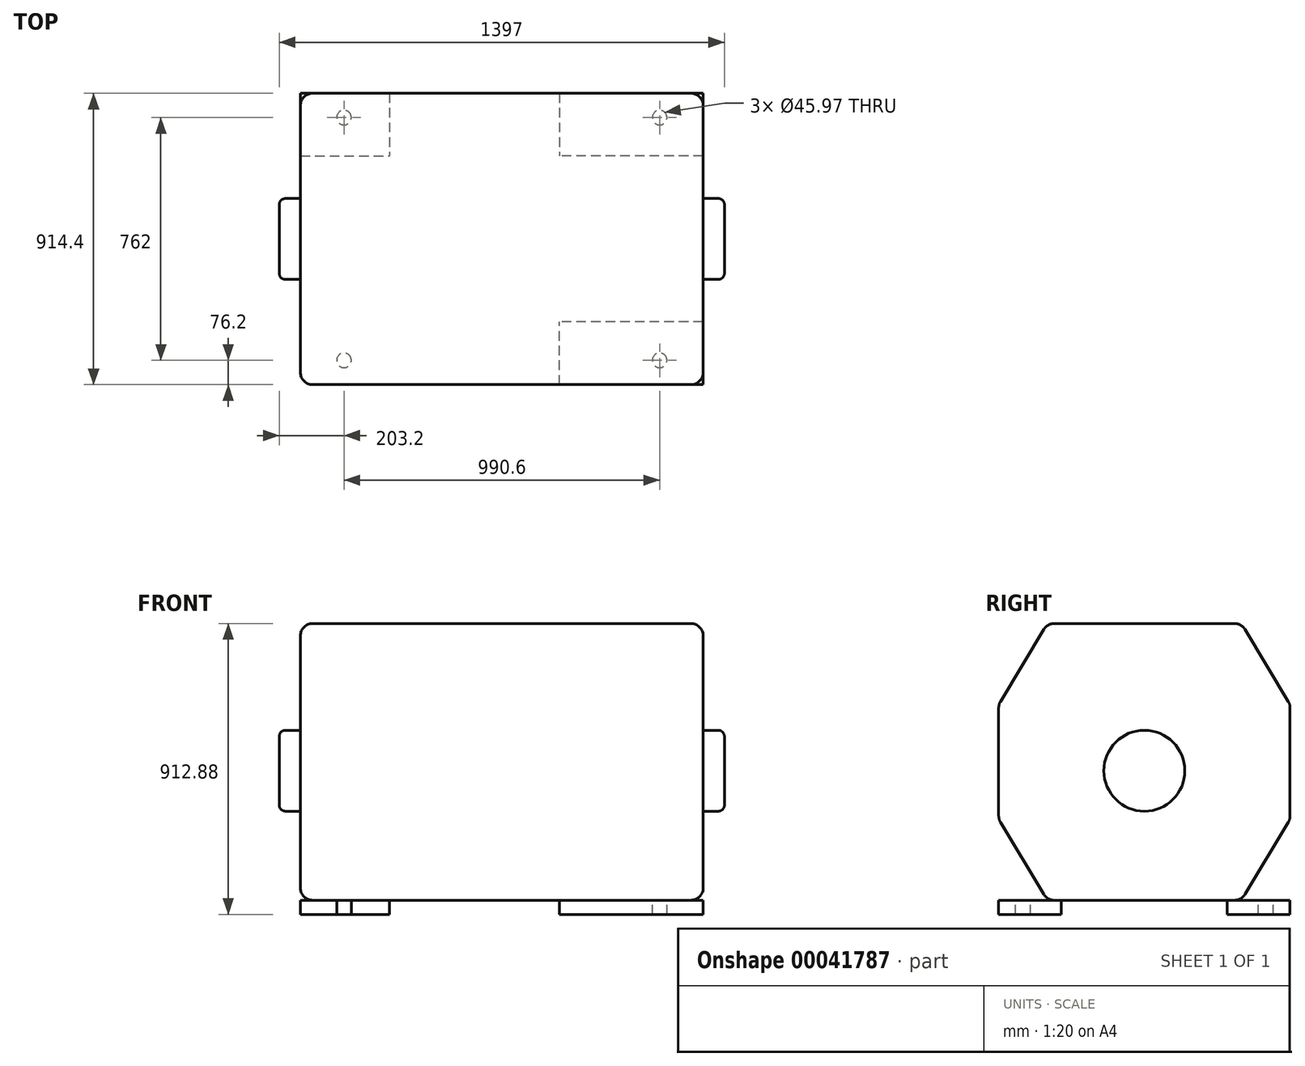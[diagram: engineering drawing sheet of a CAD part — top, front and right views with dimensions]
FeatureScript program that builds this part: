
annotation { "Feature Type Name" : "Feature", "Feature Type Description" : "" }
export const myFeature = defineFeature(function(context is Context, id is Id, definition is map)
    precondition{}
    {
        {
            var Q0;
            Q0=qCreatedBy(makeId("Top.planeOp"),FACE);
            var sketch = newSketch(context, id + "F0", { "sketchPlane" : qUnion([Q0])});
            skLineSegment(sketch, "E0.rect.bottom", {"start": v(-631.83, 457.2) * mm, "end": v(631.83, 457.2) * mm, "construction": true});
            skLineSegment(sketch, "E0.rect.top", {"start": v(-631.83, -457.2) * mm, "end": v(631.83, -457.2) * mm, "construction": true});
            skLineSegment(sketch, "E0.rect.left", {"start": v(-631.82, 457.2) * mm, "end": v(-631.83, -457.2) * mm, "construction": true});
            skLineSegment(sketch, "E0.rect.right", {"start": v(631.83, 457.2) * mm, "end": v(631.83, -457.2) * mm, "construction": true});
            skPoint(sketch, "E0.rect.middle", {"position": v(0, 0) * mm});
            skLineSegment(sketch, "E1.bottom", {"start": v(-631.83, 457.2) * mm, "end": v(-352.43, 457.2) * mm});
            skLineSegment(sketch, "E1.top", {"start": v(-631.83, 260.35) * mm, "end": v(-352.43, 260.35) * mm});
            skLineSegment(sketch, "E1.left", {"start": v(-631.83, 457.2) * mm, "end": v(-631.83, 260.35) * mm});
            skLineSegment(sketch, "E1.right", {"start": v(-352.43, 457.2) * mm, "end": v(-352.43, 260.35) * mm});
            skLineSegment(sketch, "E2.bottom", {"start": v(631.83, 457.2) * mm, "end": v(180.98, 457.2) * mm});
            skLineSegment(sketch, "E2.top", {"start": v(631.83, 260.35) * mm, "end": v(180.98, 260.35) * mm});
            skLineSegment(sketch, "E2.left", {"start": v(631.83, 457.2) * mm, "end": v(631.83, 260.35) * mm});
            skLineSegment(sketch, "E2.right", {"start": v(180.98, 457.2) * mm, "end": v(180.98, 260.35) * mm});
            skLineSegment(sketch, "E3", {"start": v(0, 476.86) * mm, "end": v(0, -472.8) * mm, "construction": true});
            skLineSegment(sketch, "E4", {"start": v(-689.14, 0) * mm, "end": v(696.03, 0) * mm, "construction": true});
            skPoint(sketch, "E4.endSnap0", {"position": v(631.83, 0) * mm});
            skLineSegment(sketch, "E5.0", {"start": v(-495.3, 476.86) * mm, "end": v(-495.3, -472.8) * mm, "construction": true});
            skLineSegment(sketch, "E6.0", {"start": v(-689.14, 381) * mm, "end": v(696.03, 381) * mm, "construction": true});
            skCircle(sketch, "E7", {"center": v(-495.3, 381) * mm, "radius": 22.99 * mm});
            skCircle(sketch, "E8.MirrorC", {"center": v(495.3, 381) * mm, "radius": 22.99 * mm});
            skCircle(sketch, "E9.MirrorC", {"center": v(-495.3, -381) * mm, "radius": 22.99 * mm});
            skLineSegment(sketch, "E10.MirrorCS", {"start": v(-631.83, -457.2) * mm, "end": v(-631.83, -260.35) * mm});
            skLineSegment(sketch, "E11.MirrorCS", {"start": v(-631.83, -260.35) * mm, "end": v(-352.43, -260.35) * mm});
            skLineSegment(sketch, "E12.MirrorCS", {"start": v(-352.43, -457.2) * mm, "end": v(-352.43, -260.35) * mm});
            skLineSegment(sketch, "E13.MirrorCS", {"start": v(-631.83, -457.2) * mm, "end": v(-352.43, -457.2) * mm});
            skLineSegment(sketch, "E14.MirrorCS", {"start": v(631.83, -457.2) * mm, "end": v(180.98, -457.2) * mm});
            skLineSegment(sketch, "E15.MirrorCS", {"start": v(631.83, -260.35) * mm, "end": v(180.98, -260.35) * mm});
            skLineSegment(sketch, "E16.MirrorCS", {"start": v(180.98, -457.2) * mm, "end": v(180.98, -260.35) * mm});
            skLineSegment(sketch, "E17.MirrorCS", {"start": v(631.83, -457.2) * mm, "end": v(631.83, -260.35) * mm});
            skLineSegment(sketch, "E18.MirrorCS", {"start": v(-631.83, -457.2) * mm, "end": v(631.83, -457.2) * mm});
            skLineSegment(sketch, "E19.MirrorCS", {"start": v(-689.14, -381) * mm, "end": v(696.03, -381) * mm, "construction": true});
            skCircle(sketch, "E20.MirrorC", {"center": v(495.3, -381) * mm, "radius": 22.99 * mm});
            skSolve(sketch);
        }
        {
            var Q0;
            Q0=makeQuery(id+"F0.imprint","IMPRINT",FACE,{"disambiguationData":[TD([[makeQuery(id+"F0.imprint","IMPRINT",EDGE,{"derivedFrom":sQuery(id+"F0.wireOp",EDGE,"E1.bottom")}),-1.0]])]});
            var Q1;
            Q1=makeQuery(id+"F0.imprint","IMPRINT",FACE,{"disambiguationData":[TD([[makeQuery(id+"F0.imprint","IMPRINT",EDGE,{"derivedFrom":sQuery(id+"F0.wireOp",EDGE,"E2.bottom")}),1.0]])]});
            var Q2;
            Q2=makeQuery(id+"F0.imprint","IMPRINT",FACE,{"disambiguationData":[TD([[makeQuery(id+"F0.imprint","IMPRINT",EDGE,{"derivedFrom":sQuery(id+"F0.wireOp",EDGE,"E15.MirrorCS")}),1.0]])]});
            var Q3;
            Q3=makeQuery(id+"F0.imprint","IMPRINT",FACE,{"disambiguationData":[TD([[makeQuery(id+"F0.imprint","IMPRINT",EDGE,{"derivedFrom":sQuery(id+"F0.wireOp",EDGE,"E9.MirrorC")}),1.0]])]});
            extrude(context, id + "F1", {"entities" : qUnion([Q0, Q1, Q2, Q3]), "oppositeDirection" : true, "depth" : 44.45 * mm});
        }
        {
            var Q0;
            Q0=qCreatedBy(makeId("Top.planeOp"),FACE);
            var sketch = newSketch(context, id + "F2", { "sketchPlane" : qUnion([Q0])});
            skLineSegment(sketch, "E21.0", {"start": v(-631.83, 457.2) * mm, "end": v(-352.43, 457.2) * mm, "construction": true});
            skLineSegment(sketch, "E22.0", {"start": v(180.98, -457.2) * mm, "end": v(631.83, -457.2) * mm, "construction": true});
            skLineSegment(sketch, "E23.bottom", {"start": v(-631.83, 457.2) * mm, "end": v(631.83, 457.2) * mm});
            skLineSegment(sketch, "E23.top", {"start": v(-631.83, -457.2) * mm, "end": v(631.83, -457.2) * mm});
            skLineSegment(sketch, "E23.left", {"start": v(-631.83, 457.2) * mm, "end": v(-631.83, -457.2) * mm});
            skLineSegment(sketch, "E23.right", {"start": v(631.83, 457.2) * mm, "end": v(631.83, -457.2) * mm});
            skSolve(sketch);
        }
        {
            var Q0;
            Q0=makeQuery(id+"F2.imprint","IMPRINT",FACE,{"disambiguationData":[TD([[makeQuery(id+"F2.imprint","IMPRINT",EDGE,{"derivedFrom":sQuery(id+"F2.wireOp",EDGE,"E23.bottom")}),-1.0]])]});
            extrude(context, id + "F3", {"entities" : qUnion([Q0]), "depth" : 868.43 * mm});
        }
        {
            var Q0;
            Q0=makeQuery(id+"F3.opExtrude","CAP_EDGE",EDGE,{"disambiguationData":[OSD([sQuery(id+"F2.wireOp",EDGE,"E23.top")])],"isStart":false});
            var Q1;
            Q1=makeQuery(id+"F3.opExtrude","CAP_EDGE",EDGE,{"disambiguationData":[OSD([sQuery(id+"F2.wireOp",EDGE,"E23.top")])],"isStart":true});
            var Q2;
            Q2=makeQuery(id+"F3.opExtrude","CAP_EDGE",EDGE,{"disambiguationData":[OSD([sQuery(id+"F2.wireOp",EDGE,"E23.bottom")])],"isStart":false});
            var Q3;
            Q3=makeQuery(id+"F3.opExtrude","CAP_EDGE",EDGE,{"disambiguationData":[OSD([sQuery(id+"F2.wireOp",EDGE,"E23.bottom")])],"isStart":true});
            chamfer(context, id + "F4", {"entities" : qUnion([Q0, Q1, Q2, Q3]), "chamferType" : ChamferType.TWO_OFFSETS, "width1" : 152.4 * mm, "oppositeDirection" : false, "width2" : 254 * mm, "tangentPropagation" : true});
        }
        {
            var Q0;
            Q0=makeQuery(id+"F3.opExtrude","SWEPT_FACE",FACE,{"disambiguationData":[OSD([sQuery(id+"F2.wireOp",EDGE,"E23.left")])]});
            var Q1;
            Q1=makeQuery(id+"F3.opExtrude","SWEPT_FACE",FACE,{"disambiguationData":[OSD([sQuery(id+"F2.wireOp",EDGE,"E23.right")])]});
            var Q2;
            {var subQ0=sQuery(id+"F2.wireOp",EDGE,"E23.bottom");Q2=makeQuery(id+"F4.opChamfer","BLEND_EDGE",EDGE,{"blendedFrom":[makeQuery(id+"F3.opExtrude","CAP_EDGE",EDGE,{"disambiguationData":[OSD([subQ0])],"isStart":true}),makeQuery(id+"F3.opExtrude","CAP_FACE",FACE,{"disambiguationData":[OSD([subQ0,sQuery(id+"F2.wireOp",EDGE,"E23.top"),sQuery(id+"F2.wireOp",EDGE,"E23.left"),sQuery(id+"F2.wireOp",EDGE,"E23.right")])],"isStart":true})],"blendedInto":[makeQuery(id+"F3.opExtrude","CAP_FACE",FACE,{"disambiguationData":[OSD([subQ0,sQuery(id+"F2.wireOp",EDGE,"E23.top"),sQuery(id+"F2.wireOp",EDGE,"E23.left"),sQuery(id+"F2.wireOp",EDGE,"E23.right")])],"isStart":true})]});}
            var Q3;
            {var subQ0=sQuery(id+"F2.wireOp",EDGE,"E23.bottom");Q3=makeQuery(id+"F4.opChamfer","BLEND_EDGE",EDGE,{"blendedFrom":[makeQuery(id+"F3.opExtrude","CAP_EDGE",EDGE,{"disambiguationData":[OSD([subQ0])],"isStart":true}),makeQuery(id+"F3.opExtrude","SWEPT_FACE",FACE,{"disambiguationData":[OSD([subQ0])]})],"blendedInto":[makeQuery(id+"F3.opExtrude","SWEPT_FACE",FACE,{"disambiguationData":[OSD([subQ0])]})]});}
            var Q4;
            Q4=makeQuery(id+"F3.opExtrude","SWEPT_FACE",FACE,{"disambiguationData":[OSD([sQuery(id+"F2.wireOp",EDGE,"E23.bottom")])]});
            var Q5;
            {var subQ0=sQuery(id+"F2.wireOp",EDGE,"E23.bottom");Q5=makeQuery(id+"F4.opChamfer","BLEND_FACE",FACE,{"disambiguationData":[OSD([subQ0]),TDD([makeQuery(id+"F3.opExtrude","CAP_EDGE",EDGE,{"disambiguationData":[OSD([subQ0])],"isStart":false})])]});}
            var Q6;
            Q6=makeQuery(id+"F3.opExtrude","CAP_FACE",FACE,{"disambiguationData":[OSD([sQuery(id+"F2.wireOp",EDGE,"E23.bottom"),sQuery(id+"F2.wireOp",EDGE,"E23.top"),sQuery(id+"F2.wireOp",EDGE,"E23.left"),sQuery(id+"F2.wireOp",EDGE,"E23.right")])],"isStart":false});
            var Q7;
            {var subQ0=sQuery(id+"F2.wireOp",EDGE,"E23.top");Q7=makeQuery(id+"F4.opChamfer","BLEND_FACE",FACE,{"disambiguationData":[OSD([subQ0]),TDD([makeQuery(id+"F3.opExtrude","CAP_EDGE",EDGE,{"disambiguationData":[OSD([subQ0])],"isStart":false})])]});}
            var Q8;
            Q8=makeQuery(id+"F3.opExtrude","SWEPT_FACE",FACE,{"disambiguationData":[OSD([sQuery(id+"F2.wireOp",EDGE,"E23.top")])]});
            var Q9;
            {var subQ0=sQuery(id+"F2.wireOp",EDGE,"E23.top");Q9=makeQuery(id+"F4.opChamfer","BLEND_FACE",FACE,{"disambiguationData":[OSD([subQ0]),TDD([makeQuery(id+"F3.opExtrude","CAP_EDGE",EDGE,{"disambiguationData":[OSD([subQ0])],"isStart":true})])]});}
            fillet(context, id + "F5", {"entities" : qUnion([Q0, Q1, Q2, Q3, Q4, Q5, Q6, Q7, Q8, Q9]), "radius" : 38.1 * mm, "tangentPropagation" : true, "allowEdgeOverflow" : false});
        }
        {
            var Q0;
            Q0=makeQuery(id+"F3.opExtrude","SWEPT_FACE",FACE,{"disambiguationData":[OSD([sQuery(id+"F2.wireOp",EDGE,"E23.right")])]});
            var sketch = newSketch(context, id + "F6", { "sketchPlane" : qUnion([Q0])});
            skLineSegment(sketch, "E24.0", {"start": v(-457.2, -44.45) * mm, "end": v(-260.35, -44.45) * mm, "construction": true});
            skLineSegment(sketch, "E25", {"start": v(0, 0) * mm, "end": v(0, 978.78) * mm, "construction": true});
            skLineSegment(sketch, "E26.0", {"start": v(-457.2, 406.4) * mm, "end": v(0, 406.4) * mm, "construction": true});
            skCircle(sketch, "E27", {"center": v(0, 406.4) * mm, "radius": 127 * mm});
            skSolve(sketch);
        }
        {
            var Q0;
            Q0=qSketchRegion(id+"F6",true);
            extrude(context, id + "F7", {"entities" : qUnion([Q0]), "depth" : 66.67 * mm});
        }
        {
            var Q0;
            Q0=makeQuery(id+"F7.opExtrude","SWEPT_BODY",BODY,{"disambiguationData":[OSD([sQuery(id+"F6.wireOp",EDGE,"E27")])]});
            var Q1;
            Q1=qCreatedBy(makeId("Right.planeOp"),FACE);
            mirror(context, id + "F8", {"operationType" : NewBodyOperationType.ADD, "entities" : qUnion([Q0]), "mirrorPlane" : qUnion([Q1])});
        }
        {
            var Q0;
            Q0=makeQuery(id+"F7.opExtrude","CAP_EDGE",EDGE,{"disambiguationData":[OSD([sQuery(id+"F6.wireOp",EDGE,"E27")])],"isStart":true});
            var Q1;
            Q1=makeQuery(id+"F7.opExtrude","CAP_EDGE",EDGE,{"disambiguationData":[OSD([sQuery(id+"F6.wireOp",EDGE,"E27")])],"isStart":false});
            var Q2;
            Q2=makeQuery(id+"F8.opPattern","COPY",EDGE,{"derivedFrom":makeQuery(id+"F7.opExtrude","CAP_EDGE",EDGE,{"disambiguationData":[OSD([sQuery(id+"F6.wireOp",EDGE,"E27")])],"isStart":false}),"instanceName":"1"});
            var Q3;
            Q3=makeQuery(id+"F8.opPattern","COPY",EDGE,{"derivedFrom":makeQuery(id+"F7.opExtrude","CAP_EDGE",EDGE,{"disambiguationData":[OSD([sQuery(id+"F6.wireOp",EDGE,"E27")])],"isStart":true}),"instanceName":"1"});
            fillet(context, id + "F9", {"entities" : qUnion([Q0, Q1, Q2, Q3]), "radius" : 19.05 * mm, "tangentPropagation" : true, "allowEdgeOverflow" : false});
        }
        {
            var Q0;
            Q0=makeQuery(id+"F7.opExtrude","CAP_FACE",FACE,{"disambiguationData":[OSD([sQuery(id+"F6.wireOp",EDGE,"E27")])],"isStart":false});
            var sketch = newSketch(context, id + "F10", { "sketchPlane" : qUnion([Q0])});
            skCircle(sketch, "E28.0.0", {"center": v(0, 406.4) * mm, "radius": 107.95 * mm, "construction": true});
            skSolve(sketch);
        }
        {
            var Q0;
            Q0=sQuery(id+"F10.wireOp",VERTEX,"E28.0.0.center");
            var Q1;
            Q1=makeQuery(id+"F1.opExtrude","SWEPT_BODY",BODY,{"disambiguationData":[OSD([sQuery(id+"F0.wireOp",EDGE,"E9.MirrorC"),sQuery(id+"F0.wireOp",EDGE,"E10.MirrorCS"),sQuery(id+"F0.wireOp",EDGE,"E11.MirrorCS"),sQuery(id+"F0.wireOp",EDGE,"E12.MirrorCS"),sQuery(id+"F0.wireOp",EDGE,"E18.MirrorCS")])]});
            hole(context, id + "F11", {"style" : HoleStyle.SIMPLE, "holeDiameter" : 127 * mm, "endStyle" : HoleEndStyle.THROUGH, "locations" : qUnion([Q0]), "scope" : qUnion([Q1])});
        }
    });
